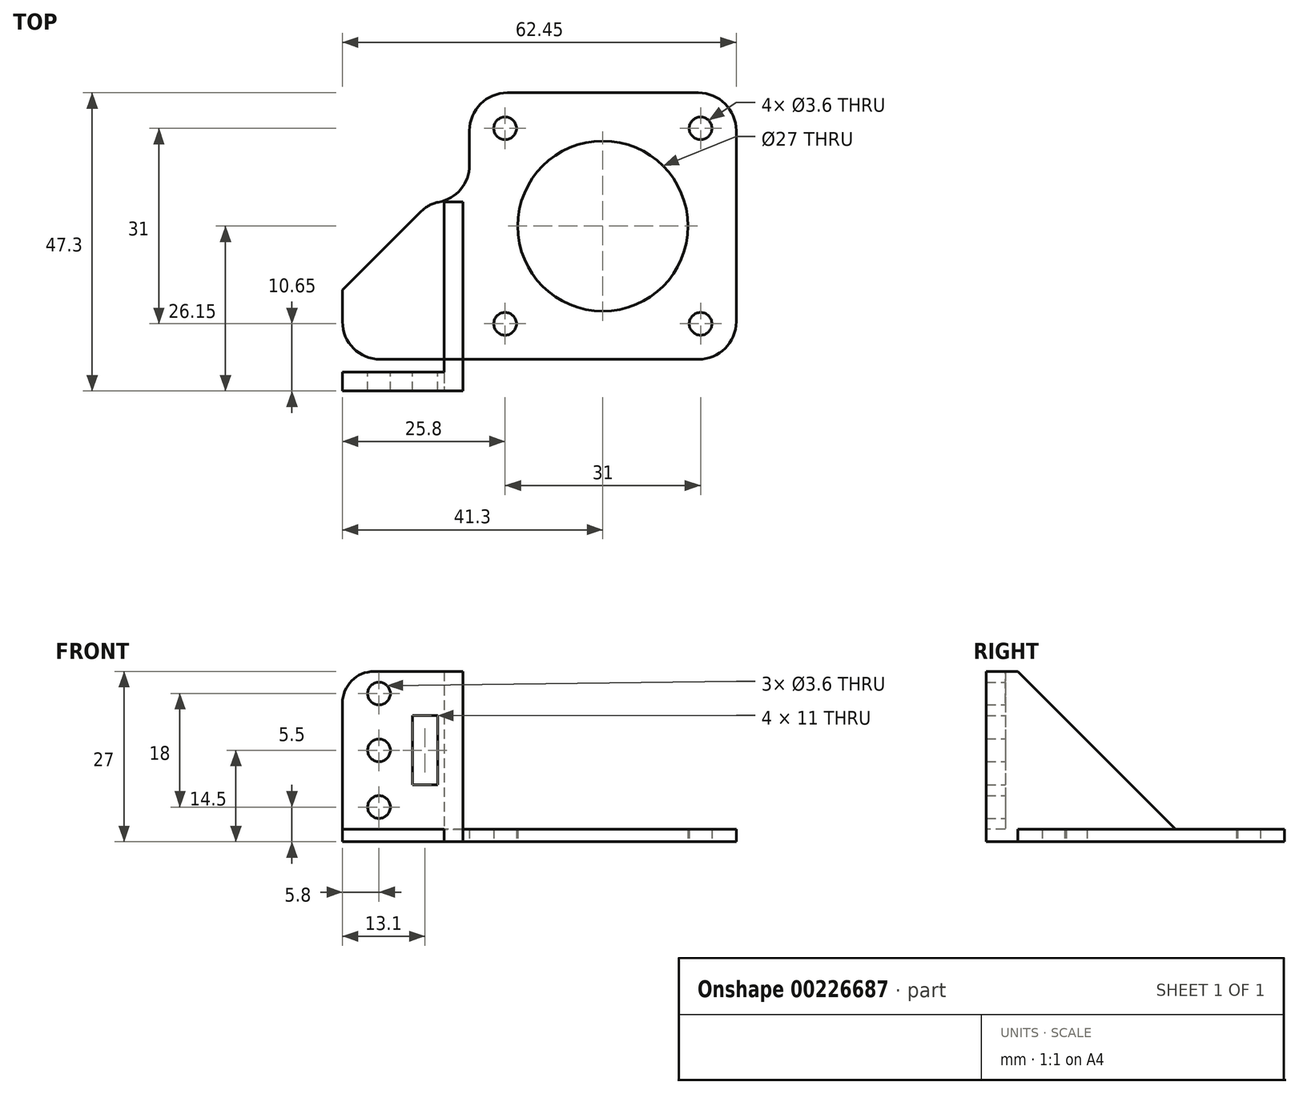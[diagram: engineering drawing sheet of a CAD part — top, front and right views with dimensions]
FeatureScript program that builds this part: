
annotation { "Feature Type Name" : "Feature", "Feature Type Description" : "" }
export const myFeature = defineFeature(function(context is Context, id is Id, definition is map)
    precondition{}
    {
        {
            var Q0;
            Q0=qCreatedBy(makeId("Top.planeOp"),FACE);
            var sketch = newSketch(context, id + "F0", { "sketchPlane" : qUnion([Q0])});
            skLineSegment(sketch, "E0.bottom", {"start": v(21.15, 21.15) * mm, "end": v(-21.15, 21.15) * mm});
            skLineSegment(sketch, "E0.top", {"start": v(21.15, -21.15) * mm, "end": v(-21.15, -21.15) * mm});
            skLineSegment(sketch, "E0.left", {"start": v(21.15, 21.15) * mm, "end": v(21.15, -21.15) * mm});
            skLineSegment(sketch, "E0.right", {"start": v(-21.15, 21.15) * mm, "end": v(-21.15, -21.15) * mm});
            skPoint(sketch, "E0.middle", {"position": v(0, 0) * mm});
            skLineSegment(sketch, "E1.bottom", {"start": v(15.5, 15.5) * mm, "end": v(-15.5, 15.5) * mm, "construction": true});
            skLineSegment(sketch, "E1.top", {"start": v(15.5, -15.5) * mm, "end": v(-15.5, -15.5) * mm, "construction": true});
            skLineSegment(sketch, "E1.left", {"start": v(15.5, 15.5) * mm, "end": v(15.5, -15.5) * mm, "construction": true});
            skLineSegment(sketch, "E1.right", {"start": v(-15.5, 15.5) * mm, "end": v(-15.5, -15.5) * mm, "construction": true});
            skCircle(sketch, "E2", {"center": v(-15.5, 15.5) * mm, "radius": 1.8 * mm});
            skCircle(sketch, "E3", {"center": v(15.5, 15.5) * mm, "radius": 1.8 * mm});
            skCircle(sketch, "E4", {"center": v(15.5, -15.5) * mm, "radius": 1.8 * mm});
            skCircle(sketch, "E5", {"center": v(-15.5, -15.5) * mm, "radius": 1.8 * mm});
            skCircle(sketch, "E6", {"center": v(0, 0) * mm, "radius": 13.5 * mm});
            skLineSegment(sketch, "E7.bottom", {"start": v(-21.15, -21.15) * mm, "end": v(-41.3, -21.15) * mm});
            skLineSegment(sketch, "E7.top", {"start": v(-21.15, 3.85) * mm, "end": v(-41.3, 3.85) * mm});
            skLineSegment(sketch, "E7.left", {"start": v(-21.15, -21.15) * mm, "end": v(-21.15, 3.85) * mm});
            skLineSegment(sketch, "E7.right", {"start": v(-41.3, -21.15) * mm, "end": v(-41.3, 3.85) * mm});
            skLineSegment(sketch, "E8.bottom", {"start": v(-41.3, -21.15) * mm, "end": v(-21.16, -21.15) * mm});
            skLineSegment(sketch, "E8.top", {"start": v(-41.3, -26.15) * mm, "end": v(-21.16, -26.15) * mm});
            skLineSegment(sketch, "E8.left", {"start": v(-41.3, -21.15) * mm, "end": v(-41.3, -26.15) * mm});
            skLineSegment(sketch, "E8.right", {"start": v(-21.16, -21.15) * mm, "end": v(-21.16, -26.15) * mm});
            skSolve(sketch);
        }
        {
            var Q0;
            Q0=makeQuery(id+"F0.imprint","IMPRINT",FACE,{"disambiguationData":[TD([[makeQuery(id+"F0.imprint","IMPRINT",EDGE,{"derivedFrom":sQuery(id+"F0.wireOp",EDGE,"E0.bottom")}),1.0]])]});
            var Q1;
            Q1=makeQuery(id+"F0.imprint","IMPRINT",FACE,{"disambiguationData":[TD([[makeQuery(id+"F0.imprint","IMPRINT",EDGE,{"derivedFrom":sQuery(id+"F0.wireOp",EDGE,"E7.bottom")}),-1.0]])]});
            var Q2;
            Q2=makeQuery(id+"F0.imprint","IMPRINT",FACE,{"disambiguationData":[TD([[makeQuery(id+"F0.imprint","IMPRINT",EDGE,{"derivedFrom":sQuery(id+"F0.wireOp",EDGE,"E8.bottom")}),-1.0]])]});
            extrude(context, id + "F1", {"entities" : qUnion([Q0, Q1, Q2]), "offsetDistance" : 25 * mm, "depth" : 2 * mm});
        }
        {
            var Q0;
            Q0=qCreatedBy(makeId("Top.planeOp"),FACE);
            var sketch = newSketch(context, id + "F2", { "sketchPlane" : qUnion([Q0])});
            skLineSegment(sketch, "E9.bottom", {"start": v(-22.16, 3.85) * mm, "end": v(-25.16, 3.85) * mm});
            skLineSegment(sketch, "E9.top", {"start": v(-22.16, -26.15) * mm, "end": v(-25.16, -26.15) * mm});
            skLineSegment(sketch, "E9.left", {"start": v(-22.16, 3.85) * mm, "end": v(-22.16, -26.15) * mm});
            skLineSegment(sketch, "E9.right", {"start": v(-25.16, 3.85) * mm, "end": v(-25.16, -26.15) * mm});
            skSolve(sketch);
        }
        {
            var Q0;
            Q0=qSketchRegion(id+"F2",true);
            extrude(context, id + "F3", {"entities" : qUnion([Q0]), "operationType" : NewBodyOperationType.ADD, "depth" : 27 * mm});
        }
        {
            var Q0;
            {var subQ0=sQuery(id+"F0.wireOp",EDGE,"E8.left");var subQ1=sQuery(id+"F0.wireOp",EDGE,"E7.right");var subQ2=sQuery(id+"F0.wireOp",EDGE,"E8.top");var subQ3=sQuery(id+"F0.wireOp",EDGE,"E7.top");Q0=makeQuery(id+"F3.boolean.opBoolean","SPLIT",FACE,{"disambiguationData":[TD([makeQuery(id+"F3.opExtrude","SWEPT_FACE",FACE,{"disambiguationData":[OSD([sQuery(id+"F2.wireOp",EDGE,"E9.right")])]})])],"derivedFrom":makeQuery(id+"F1.opExtrude","CAP_FACE",FACE,{"disambiguationData":[OSD([sQuery(id+"F0.wireOp",EDGE,"E0.bottom"),sQuery(id+"F0.wireOp",EDGE,"E0.top"),sQuery(id+"F0.wireOp",EDGE,"E0.left"),sQuery(id+"F0.wireOp",EDGE,"E0.right"),sQuery(id+"F0.wireOp",EDGE,"E2"),sQuery(id+"F0.wireOp",EDGE,"E3"),sQuery(id+"F0.wireOp",EDGE,"E4"),sQuery(id+"F0.wireOp",EDGE,"E5"),sQuery(id+"F0.wireOp",EDGE,"E6"),sQuery(id+"F0.wireOp",EDGE,"E7.bottom"),subQ3,subQ1,subQ2,subQ0,sQuery(id+"F0.wireOp",EDGE,"E8.right")])],"isStart":false})});}
            var sketch = newSketch(context, id + "F4", { "sketchPlane" : qUnion([Q0])});
            skLineSegment(sketch, "E10.bottom", {"start": v(-41.3, -23.15) * mm, "end": v(-25.16, -23.15) * mm});
            skLineSegment(sketch, "E10.top", {"start": v(-41.3, -26.15) * mm, "end": v(-25.16, -26.15) * mm});
            skLineSegment(sketch, "E10.left", {"start": v(-41.3, -23.15) * mm, "end": v(-41.3, -26.15) * mm});
            skLineSegment(sketch, "E10.right", {"start": v(-25.16, -23.15) * mm, "end": v(-25.16, -26.15) * mm});
            skSolve(sketch);
        }
        {
            var Q0;
            Q0=makeQuery(id+"F4.imprint","IMPRINT",FACE,{"disambiguationData":[TD([[makeQuery(id+"F4.imprint","IMPRINT",EDGE,{"derivedFrom":sQuery(id+"F4.wireOp",EDGE,"E10.bottom")}),-1.0]])]});
            extrude(context, id + "F5", {"entities" : qUnion([Q0]), "operationType" : NewBodyOperationType.ADD, "depth" : 25 * mm});
        }
        {
            var Q0;
            Q0=makeQuery(id+"F5.opExtrude","SWEPT_FACE",FACE,{"disambiguationData":[OSD([sQuery(id+"F4.wireOp",EDGE,"E10.bottom")])]});
            var sketch = newSketch(context, id + "F6", { "sketchPlane" : qUnion([Q0])});
            skCircle(sketch, "E11", {"center": v(35.5, 14.5) * mm, "radius": 1.8 * mm});
            skCircle(sketch, "E12", {"center": v(35.5, 5.5) * mm, "radius": 1.8 * mm});
            skCircle(sketch, "E13", {"center": v(35.5, 23.5) * mm, "radius": 1.8 * mm});
            skLineSegment(sketch, "E14.bottom", {"start": v(30.2, 20) * mm, "end": v(26.2, 20) * mm});
            skLineSegment(sketch, "E14.top", {"start": v(30.2, 9) * mm, "end": v(26.2, 9) * mm});
            skLineSegment(sketch, "E14.left", {"start": v(30.2, 20) * mm, "end": v(30.2, 9) * mm});
            skLineSegment(sketch, "E14.right", {"start": v(26.2, 20) * mm, "end": v(26.2, 9) * mm});
            skSolve(sketch);
        }
        {
            var Q0;
            Q0=makeQuery(id+"F6.imprint","IMPRINT",FACE,{"disambiguationData":[TD([[makeQuery(id+"F6.imprint","IMPRINT",EDGE,{"derivedFrom":sQuery(id+"F6.wireOp",EDGE,"E11")}),1.0]])]});
            var Q1;
            Q1=makeQuery(id+"F6.imprint","IMPRINT",FACE,{"disambiguationData":[TD([[makeQuery(id+"F6.imprint","IMPRINT",EDGE,{"derivedFrom":sQuery(id+"F6.wireOp",EDGE,"E12")}),1.0]])]});
            var Q2;
            Q2=makeQuery(id+"F6.imprint","IMPRINT",FACE,{"disambiguationData":[TD([[makeQuery(id+"F6.imprint","IMPRINT",EDGE,{"derivedFrom":sQuery(id+"F6.wireOp",EDGE,"E13")}),1.0]])]});
            var Q3;
            Q3=makeQuery(id+"F6.imprint","IMPRINT",FACE,{"disambiguationData":[TD([[makeQuery(id+"F6.imprint","IMPRINT",EDGE,{"derivedFrom":sQuery(id+"F6.wireOp",EDGE,"E14.bottom")}),1.0]])]});
            extrude(context, id + "F7", {"entities" : qUnion([Q0, Q1, Q2, Q3]), "operationType" : NewBodyOperationType.REMOVE, "oppositeDirection" : true, "depth" : 25 * mm});
        }
        {
            var Q0;
            Q0=makeQuery(id+"F3.opExtrude","CAP_EDGE",EDGE,{"disambiguationData":[OSD([sQuery(id+"F2.wireOp",EDGE,"E9.bottom")])],"isStart":false});
            chamfer(context, id + "F8", {"entities" : qUnion([Q0]), "width" : 25 * mm, "tangentPropagation" : true});
        }
        {
            var Q0;
            Q0=makeQuery(id+"F1.opExtrude","SWEPT_EDGE",EDGE,{"disambiguationData":[OSD([sQuery(id+"F0.wireOp",EDGE,"E7.top"),sQuery(id+"F0.wireOp",EDGE,"E7.right")])]});
            chamfer(context, id + "F9", {"entities" : qUnion([Q0]), "width" : 14 * mm, "tangentPropagation" : true});
        }
        {
            var Q0;
            {var subQ0=sQuery(id+"F0.wireOp",EDGE,"E7.right");Q0=makeQuery(id+"F9.opChamfer","BLEND_EDGE",EDGE,{"blendedFrom":[makeQuery(id+"F1.opExtrude","SWEPT_EDGE",EDGE,{"disambiguationData":[OSD([sQuery(id+"F0.wireOp",EDGE,"E7.top"),subQ0])]}),makeQuery(id+"F5.boolean.opBoolean","MERGE",FACE,{"derivedFrom":[makeQuery(id+"F1.opExtrude","SWEPT_FACE",FACE,{"disambiguationData":[OSD([subQ0,sQuery(id+"F0.wireOp",EDGE,"E8.left")])]}),makeQuery(id+"F5.opExtrude","SWEPT_FACE",FACE,{"disambiguationData":[OSD([sQuery(id+"F4.wireOp",EDGE,"E10.left")])]})]})],"blendedInto":[makeQuery(id+"F5.boolean.opBoolean","MERGE",FACE,{"derivedFrom":[makeQuery(id+"F1.opExtrude","SWEPT_FACE",FACE,{"disambiguationData":[OSD([subQ0,sQuery(id+"F0.wireOp",EDGE,"E8.left")])]}),makeQuery(id+"F5.opExtrude","SWEPT_FACE",FACE,{"disambiguationData":[OSD([sQuery(id+"F4.wireOp",EDGE,"E10.left")])]})]})]});}
            var Q1;
            {var subQ0=sQuery(id+"F0.wireOp",EDGE,"E7.top");Q1=makeQuery(id+"F9.opChamfer","BLEND_EDGE",EDGE,{"blendedFrom":[makeQuery(id+"F1.opExtrude","SWEPT_EDGE",EDGE,{"disambiguationData":[OSD([subQ0,sQuery(id+"F0.wireOp",EDGE,"E7.right")])]}),makeQuery(id+"F3.boolean.opBoolean","MERGE",FACE,{"derivedFrom":[makeQuery(id+"F1.opExtrude","SWEPT_FACE",FACE,{"disambiguationData":[OSD([subQ0])]}),makeQuery(id+"F3.opExtrude","SWEPT_FACE",FACE,{"disambiguationData":[OSD([sQuery(id+"F2.wireOp",EDGE,"E9.bottom")])]})]})],"blendedInto":[makeQuery(id+"F3.boolean.opBoolean","MERGE",FACE,{"derivedFrom":[makeQuery(id+"F1.opExtrude","SWEPT_FACE",FACE,{"disambiguationData":[OSD([subQ0])]}),makeQuery(id+"F3.opExtrude","SWEPT_FACE",FACE,{"disambiguationData":[OSD([sQuery(id+"F2.wireOp",EDGE,"E9.bottom")])]})]})]});}
            var Q2;
            Q2=makeQuery(id+"F1.opExtrude","SWEPT_EDGE",EDGE,{"disambiguationData":[OSD([sQuery(id+"F0.wireOp",EDGE,"E8.top"),sQuery(id+"F0.wireOp",EDGE,"E8.right")])]});
            var Q3;
            Q3=makeQuery(id+"F5.opExtrude","CAP_EDGE",EDGE,{"disambiguationData":[OSD([sQuery(id+"F4.wireOp",EDGE,"E10.left")])],"isStart":false});
            fillet(context, id + "F10", {"entities" : qUnion([Q0, Q1, Q2, Q3]), "radius" : 5 * mm, "tangentPropagation" : true, "allowEdgeOverflow" : false});
        }
        {
            var Q0;
            Q0=makeQuery(id+"F1.opExtrude","SWEPT_EDGE",EDGE,{"disambiguationData":[OSD([sQuery(id+"F0.wireOp",EDGE,"E0.top"),sQuery(id+"F0.wireOp",EDGE,"E0.left")])]});
            var Q1;
            Q1=makeQuery(id+"F1.opExtrude","SWEPT_EDGE",EDGE,{"disambiguationData":[OSD([sQuery(id+"F0.wireOp",EDGE,"E0.bottom"),sQuery(id+"F0.wireOp",EDGE,"E0.left")])]});
            var Q2;
            Q2=makeQuery(id+"F1.opExtrude","SWEPT_EDGE",EDGE,{"disambiguationData":[OSD([sQuery(id+"F0.wireOp",EDGE,"E0.bottom"),sQuery(id+"F0.wireOp",EDGE,"E0.right")])]});
            var Q3;
            Q3=makeQuery(id+"F1.opExtrude","SWEPT_EDGE",EDGE,{"disambiguationData":[OSD([sQuery(id+"F0.wireOp",EDGE,"E0.right"),sQuery(id+"F0.wireOp",EDGE,"E7.top"),sQuery(id+"F0.wireOp",EDGE,"E7.left")])]});
            var Q4;
            Q4=makeQuery(id+"F1.opExtrude","SWEPT_EDGE",EDGE,{"disambiguationData":[OSD([sQuery(id+"F0.wireOp",EDGE,"E7.bottom"),sQuery(id+"F0.wireOp",EDGE,"E8.bottom"),sQuery(id+"F0.wireOp",EDGE,"E8.right")])]});
            fillet(context, id + "F11", {"entities" : qUnion([Q0, Q1, Q2, Q3, Q4]), "radius" : 6 * mm, "tangentPropagation" : true, "allowEdgeOverflow" : false});
        }
    });
